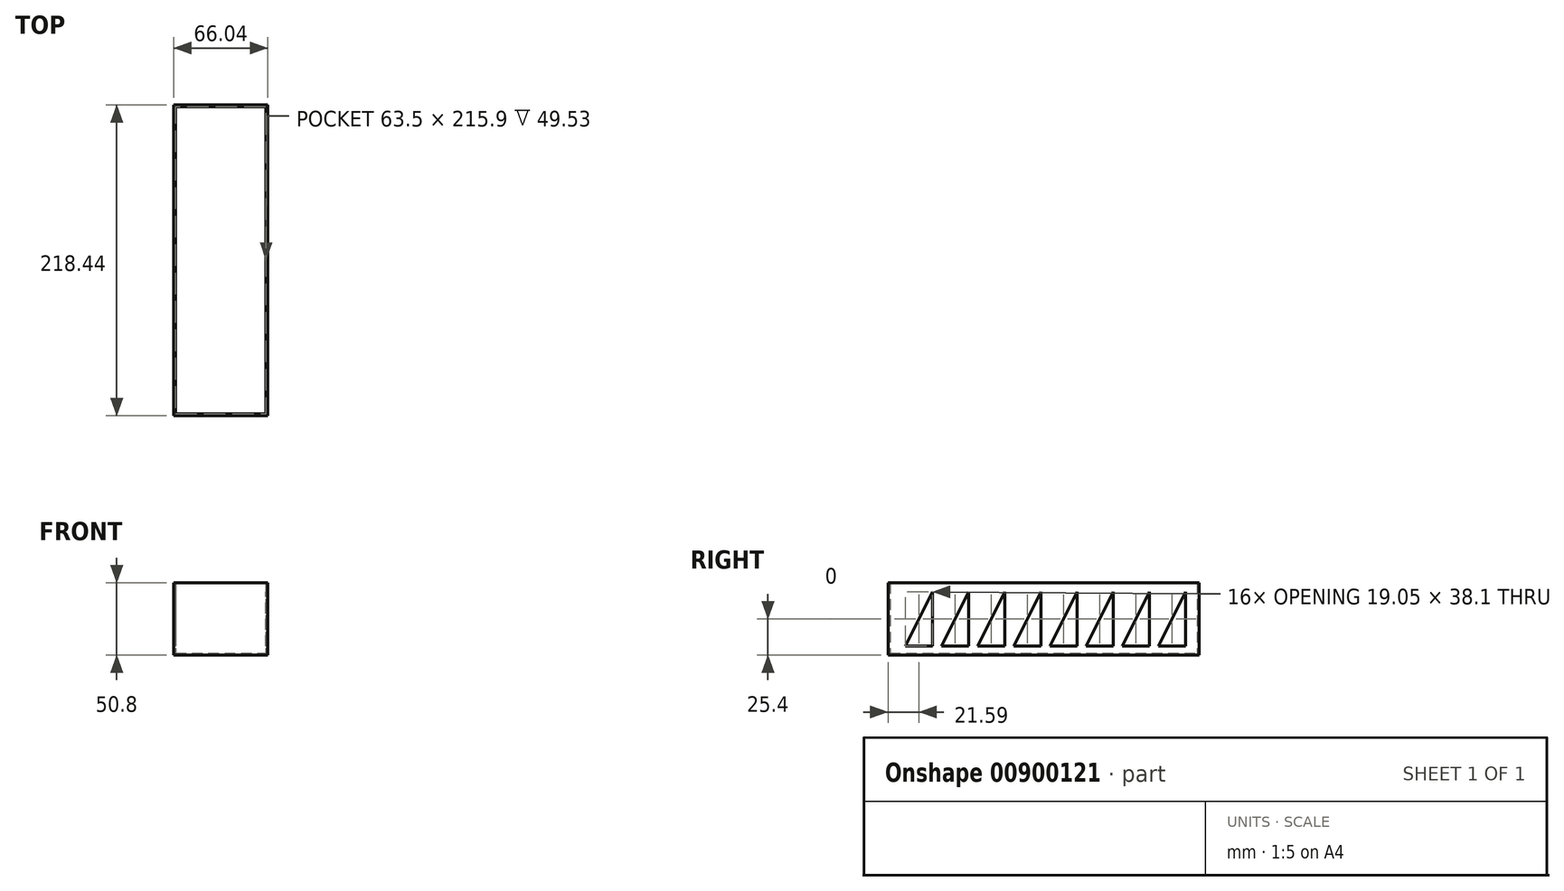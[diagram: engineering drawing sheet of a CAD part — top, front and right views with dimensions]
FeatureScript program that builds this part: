
annotation { "Feature Type Name" : "Feature", "Feature Type Description" : "" }
export const myFeature = defineFeature(function(context is Context, id is Id, definition is map)
    precondition{}
    {
        {
            var Q0;
            Q0=qCreatedBy(makeId("Top.planeOp"),FACE);
            var sketch = newSketch(context, id + "F0", { "sketchPlane" : qUnion([Q0])});
            skLineSegment(sketch, "E0.bottom", {"start": v(31.75, 107.95) * mm, "end": v(-31.75, 107.95) * mm});
            skLineSegment(sketch, "E0.top", {"start": v(31.75, -107.95) * mm, "end": v(-31.75, -107.95) * mm});
            skLineSegment(sketch, "E0.left", {"start": v(31.75, 107.95) * mm, "end": v(31.75, -107.95) * mm});
            skLineSegment(sketch, "E0.right", {"start": v(-31.75, 107.95) * mm, "end": v(-31.75, -107.95) * mm});
            skPoint(sketch, "E0.middle", {"position": v(0, 0) * mm});
            skLineSegment(sketch, "E1.0", {"start": v(33.02, 109.22) * mm, "end": v(-33.02, 109.22) * mm});
            skLineSegment(sketch, "E1.1", {"start": v(33.02, 109.22) * mm, "end": v(33.02, -109.22) * mm});
            skLineSegment(sketch, "E1.2", {"start": v(33.02, -109.22) * mm, "end": v(-33.02, -109.22) * mm});
            skLineSegment(sketch, "E1.3", {"start": v(-33.02, 109.22) * mm, "end": v(-33.02, -109.22) * mm});
            skSolve(sketch);
        }
        {
            var Q0;
            Q0=qSketchRegion(id+"F0",true);
            var Q1;
            Q1=makeQuery(id+"F0.imprint","IMPRINT",FACE,{"disambiguationData":[TD([[makeQuery(id+"F0.imprint","IMPRINT",EDGE,{"derivedFrom":sQuery(id+"F0.wireOp",EDGE,"E0.bottom")}),1.0]])]});
            extrude(context, id + "F1", {"entities" : qUnion([Q0, Q1]), "depth" : 1.27 * mm, "offsetDistance" : 25.4 * mm});
        }
        {
            var Q0;
            Q0=qSketchRegion(id+"F0",true);
            extrude(context, id + "F2", {"entities" : qUnion([Q0]), "operationType" : NewBodyOperationType.ADD, "depth" : 50.8 * mm, "offsetDistance" : 25.4 * mm});
        }
        {
            var Q0;
            {var subQ0=sQuery(id+"F0.wireOp",EDGE,"E1.3");Q0=makeQuery(id+"F2.boolean.opBoolean","MERGE",FACE,{"derivedFrom":[makeQuery(id+"F1.opExtrude","SWEPT_FACE",FACE,{"disambiguationData":[OSD([subQ0])]}),makeQuery(id+"F2.opExtrude","SWEPT_FACE",FACE,{"disambiguationData":[OSD([subQ0])]})]});}
            var sketch = newSketch(context, id + "F3", { "sketchPlane" : qUnion([Q0])});
            skLineSegment(sketch, "E2", {"start": v(-99.7, 44.45) * mm, "end": v(-99.7, 6.35) * mm});
            skLineSegment(sketch, "E3", {"start": v(-99.7, 6.35) * mm, "end": v(-80.65, 6.35) * mm});
            skLineSegment(sketch, "E4", {"start": v(-80.64, 6.35) * mm, "end": v(-99.7, 44.45) * mm});
            skLineSegment(sketch, "E5.1.0.0", {"start": v(-55.25, 6.35) * mm, "end": v(-74.3, 44.45) * mm});
            skLineSegment(sketch, "E5.1.0.1", {"start": v(-74.3, 44.45) * mm, "end": v(-74.3, 6.35) * mm});
            skLineSegment(sketch, "E5.1.0.2", {"start": v(-74.3, 44.45) * mm, "end": v(-74.3, 44.45) * mm});
            skLineSegment(sketch, "E5.1.0.3", {"start": v(-74.3, 6.35) * mm, "end": v(-55.25, 6.35) * mm});
            skLineSegment(sketch, "E5.2.0.0", {"start": v(-29.85, 6.35) * mm, "end": v(-48.9, 44.45) * mm});
            skLineSegment(sketch, "E5.2.0.1", {"start": v(-48.9, 44.45) * mm, "end": v(-48.9, 6.35) * mm});
            skLineSegment(sketch, "E5.2.0.2", {"start": v(-48.9, 44.45) * mm, "end": v(-48.9, 44.45) * mm});
            skLineSegment(sketch, "E5.2.0.3", {"start": v(-48.9, 6.35) * mm, "end": v(-29.85, 6.35) * mm});
            skLineSegment(sketch, "E5.3.0.0", {"start": v(-4.45, 6.35) * mm, "end": v(-23.5, 44.45) * mm});
            skLineSegment(sketch, "E5.3.0.1", {"start": v(-23.5, 44.45) * mm, "end": v(-23.5, 6.35) * mm});
            skLineSegment(sketch, "E5.3.0.2", {"start": v(-23.5, 44.45) * mm, "end": v(-23.5, 44.45) * mm});
            skLineSegment(sketch, "E5.3.0.3", {"start": v(-23.5, 6.35) * mm, "end": v(-4.45, 6.35) * mm});
            skLineSegment(sketch, "E5.4.0.0", {"start": v(20.95, 6.35) * mm, "end": v(1.9, 44.45) * mm});
            skLineSegment(sketch, "E5.4.0.1", {"start": v(1.9, 44.45) * mm, "end": v(1.9, 6.35) * mm});
            skLineSegment(sketch, "E5.4.0.2", {"start": v(1.9, 44.45) * mm, "end": v(1.9, 44.45) * mm});
            skLineSegment(sketch, "E5.4.0.3", {"start": v(1.9, 6.35) * mm, "end": v(20.95, 6.35) * mm});
            skLineSegment(sketch, "E5.5.0.0", {"start": v(46.35, 6.35) * mm, "end": v(27.3, 44.45) * mm});
            skLineSegment(sketch, "E5.5.0.1", {"start": v(27.3, 44.45) * mm, "end": v(27.3, 6.35) * mm});
            skLineSegment(sketch, "E5.5.0.2", {"start": v(27.3, 44.45) * mm, "end": v(27.3, 44.45) * mm});
            skLineSegment(sketch, "E5.5.0.3", {"start": v(27.3, 6.35) * mm, "end": v(46.35, 6.35) * mm});
            skLineSegment(sketch, "E5.6.0.0", {"start": v(71.75, 6.35) * mm, "end": v(52.7, 44.45) * mm});
            skLineSegment(sketch, "E5.6.0.1", {"start": v(52.7, 44.45) * mm, "end": v(52.7, 6.35) * mm});
            skLineSegment(sketch, "E5.6.0.2", {"start": v(52.7, 44.45) * mm, "end": v(52.7, 44.45) * mm});
            skLineSegment(sketch, "E5.6.0.3", {"start": v(52.7, 6.35) * mm, "end": v(71.75, 6.35) * mm});
            skLineSegment(sketch, "E5.7.0.0", {"start": v(97.15, 6.35) * mm, "end": v(78.1, 44.45) * mm});
            skLineSegment(sketch, "E5.7.0.1", {"start": v(78.1, 44.45) * mm, "end": v(78.1, 6.35) * mm});
            skLineSegment(sketch, "E5.7.0.2", {"start": v(78.1, 44.45) * mm, "end": v(78.1, 44.45) * mm});
            skLineSegment(sketch, "E5.7.0.3", {"start": v(78.1, 6.35) * mm, "end": v(97.15, 6.35) * mm});
            skLineSegment(sketch, "E5.direction1", {"start": v(-80.65, 6.35) * mm, "end": v(-55.25, 6.35) * mm, "construction": true});
            skSolve(sketch);
        }
        {
            var Q0;
            Q0=qSketchRegion(id+"F3",true);
            extrude(context, id + "F4", {"entities" : qUnion([Q0]), "operationType" : NewBodyOperationType.REMOVE, "oppositeDirection" : true, "depth" : 76.2 * mm, "offsetDistance" : 25.4 * mm});
        }
    });
